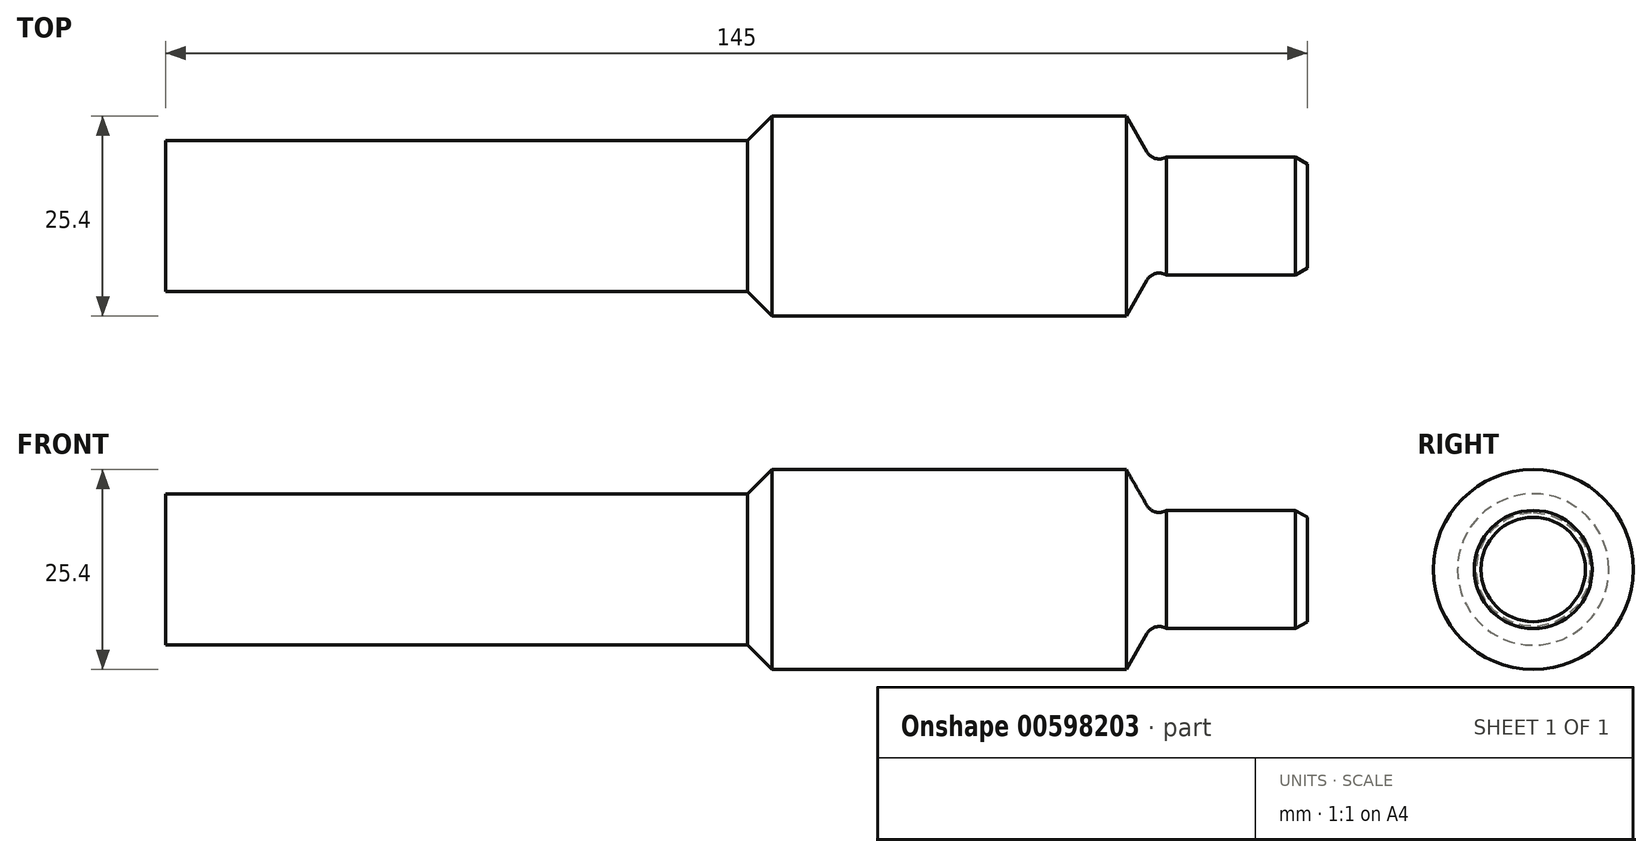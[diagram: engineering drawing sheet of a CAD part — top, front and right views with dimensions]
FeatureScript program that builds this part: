
annotation { "Feature Type Name" : "Feature", "Feature Type Description" : "" }
export const myFeature = defineFeature(function(context is Context, id is Id, definition is map)
    precondition{}
    {
        {
            var Q0;
            Q0=qCreatedBy(makeId("Front.planeOp"),FACE);
            var sketch = newSketch(context, id + "F0", { "sketchPlane" : qUnion([Q0])});
            skLineSegment(sketch, "E0", {"start": v(0, 9.61) * mm, "end": v(73.91, 9.61) * mm});
            skLineSegment(sketch, "E1", {"start": v(73.91, 9.61) * mm, "end": v(77, 12.7) * mm});
            skLineSegment(sketch, "E2", {"start": v(77, 12.7) * mm, "end": v(122, 12.7) * mm});
            skLineSegment(sketch, "E3", {"start": v(122, 12.7) * mm, "end": v(124.63, 8.14) * mm});
            skLineSegment(sketch, "E4", {"start": v(127.08, 7.5) * mm, "end": v(143.5, 7.5) * mm});
            skLineSegment(sketch, "E5", {"start": v(143.5, 7.5) * mm, "end": v(145, 6.63) * mm});
            skLineSegment(sketch, "E6", {"start": v(145, 6.63) * mm, "end": v(145, 0) * mm});
            skArc(sketch, "E7", {"start": v(124.63, 8.14) * mm, "mid": v(125.72, 7.3) * mm, "end": v(127.08, 7.5) * mm});
            skLineSegment(sketch, "E8", {"start": v(0, 9.61) * mm, "end": v(0, 0) * mm});
            skLineSegment(sketch, "E9", {"start": v(0, 0) * mm, "end": v(145, 0) * mm});
            skSolve(sketch);
        }
        {
            var Q0;
            Q0=makeQuery(id+"F0.imprint","IMPRINT",FACE,{"disambiguationData":[TD([[makeQuery(id+"F0.imprint","IMPRINT",EDGE,{"derivedFrom":sQuery(id+"F0.wireOp",EDGE,"BdXgMbgg-Zjpy-NSAW-rjV4-okTaLXoclp3I")}),-1.0]])]});
            var Q1;
            {var subQ0=sQuery(id+"F0.wireOp",EDGE,"E0");Q1=makeQuery(id+"F0.imprint","IMPRINT",FACE,{"disambiguationData":[TD([[makeQuery(id+"F0.imprint","IMPRINT",EDGE,{"derivedFrom":subQ0}),-1.0]])]});}
            var Q2;
            Q2=sQuery(id+"F0.wireOp",EDGE,"E9");
            revolve(context, id + "F1", {"entities" : qUnion([Q0, Q1]), "axis" : qUnion([Q2]), "revolveType" : RevolveType.FULL});
        }
    });
